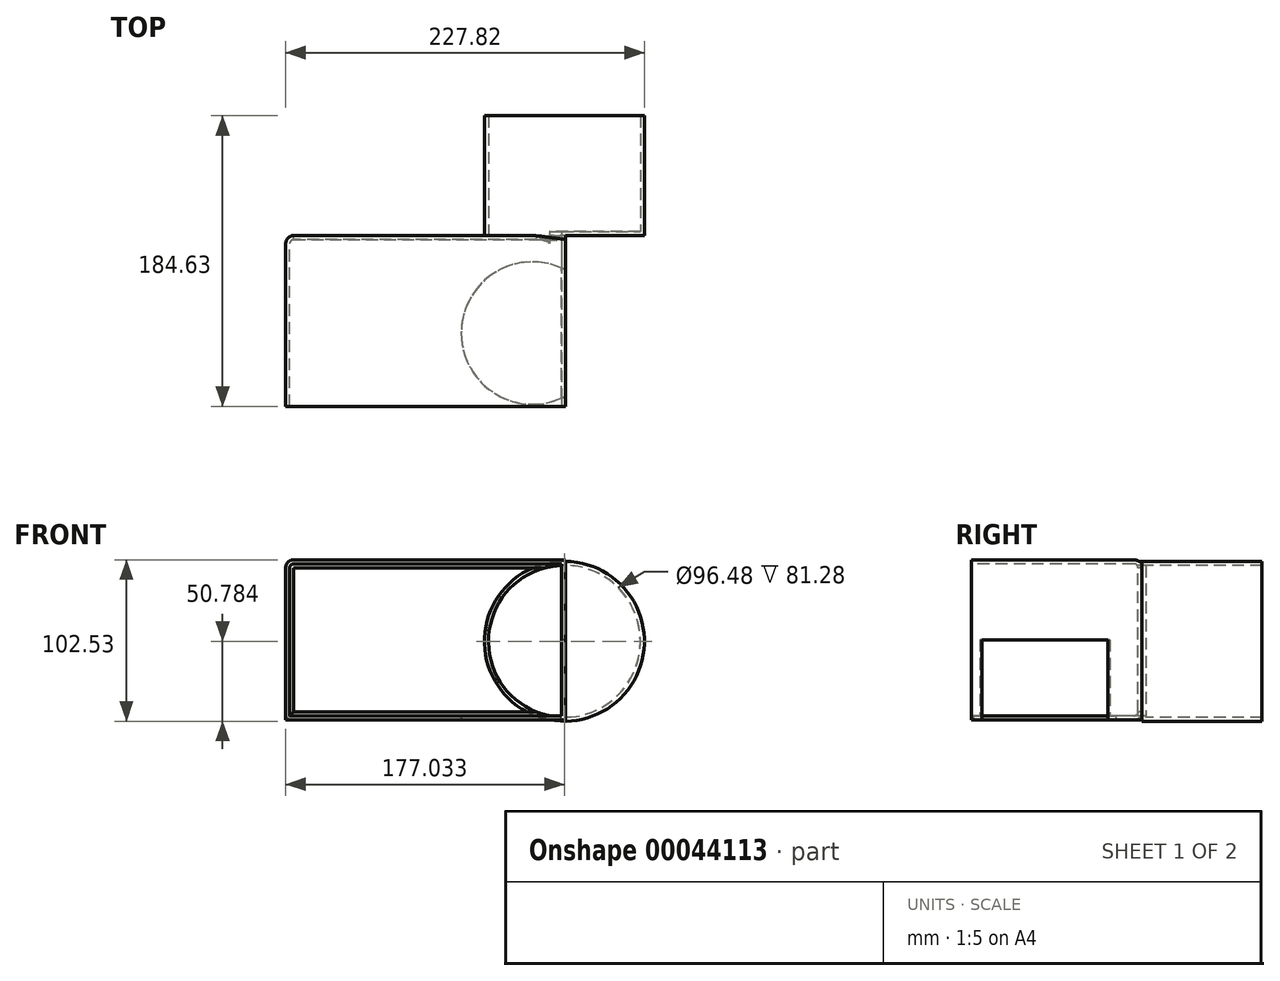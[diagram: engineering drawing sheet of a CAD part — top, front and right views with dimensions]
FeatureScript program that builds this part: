
annotation { "Feature Type Name" : "Feature", "Feature Type Description" : "" }
export const myFeature = defineFeature(function(context is Context, id is Id, definition is map)
    precondition{}
    {
        {
            var Q0;
            Q0=qCreatedBy(makeId("Top.planeOp"),FACE);
            var sketch = newSketch(context, id + "F0", { "sketchPlane" : qUnion([Q0])});
            skLineSegment(sketch, "E0.bottom", {"start": v(-163, 108.43) * mm, "end": v(14.8, 108.43) * mm});
            skLineSegment(sketch, "E0.top", {"start": v(-163, 0) * mm, "end": v(14.8, 0) * mm});
            skLineSegment(sketch, "E0.left", {"start": v(-163, 108.43) * mm, "end": v(-163, 0) * mm});
            skLineSegment(sketch, "E0.right", {"start": v(14.8, 108.43) * mm, "end": v(14.8, 0) * mm});
            skSolve(sketch);
        }
        {
            var Q0;
            Q0=makeQuery(id+"F0.imprint","IMPRINT",FACE,{"disambiguationData":[TD([[makeQuery(id+"F0.imprint","IMPRINT",EDGE,{"derivedFrom":sQuery(id+"F0.wireOp",EDGE,"E0.bottom")}),-1.0]])]});
            extrude(context, id + "F1", {"entities" : qUnion([Q0]), "depth" : 101.6 * mm});
        }
        {
            var Q0;
            Q0=makeQuery(id+"F1.opExtrude","SWEPT_FACE",FACE,{"disambiguationData":[OSD([sQuery(id+"F0.wireOp",EDGE,"E0.bottom")])]});
            var sketch = newSketch(context, id + "F2", { "sketchPlane" : qUnion([Q0])});
            skCircle(sketch, "E1", {"center": v(-14.03, 49.85) * mm, "radius": 50.78 * mm});
            skSolve(sketch);
        }
        {
            var Q0;
            Q0 = qSketchRegion(id + "F2", true);
            extrude(context, id + "F3", {"entities" : qUnion([Q0]), "operationType" : NewBodyOperationType.ADD, "depth" : 76.2 * mm});
        }
        {
            var Q0;
            Q0=makeQuery(id+"F1.opExtrude","CAP_FACE",FACE,{"disambiguationData":[OSD([sQuery(id+"F0.wireOp",EDGE,"E0.bottom"),sQuery(id+"F0.wireOp",EDGE,"E0.top"),sQuery(id+"F0.wireOp",EDGE,"E0.left"),sQuery(id+"F0.wireOp",EDGE,"E0.right")])],"isStart":false});
            var sketch = newSketch(context, id + "F4", { "sketchPlane" : qUnion([Q0])});
            skFitSpline(sketch, "E2", {"points": [v(-81.6, 66.74) * mm, v(-20.34, 86.26) * mm, v(95.36, 39.43) * mm, v(-128.5, 14.59) * mm, v(-81.6, 66.74) * mm]});
            skLineSegment(sketch, "E3", {"start": v(-20.38, 79.14) * mm, "end": v(-20.38, 54.21) * mm, "construction": true});
            skPoint(sketch, "E3.endSnap0", {"position": v(14.8, 54.21) * mm});
            skSolve(sketch);
        }
        {
            var Q0;
            Q0=makeQuery(id+"F1.opExtrude","CAP_EDGE",EDGE,{"disambiguationData":[OSD([sQuery(id+"F0.wireOp",EDGE,"E0.left")])],"isStart":false});
            var Q1;
            Q1=makeQuery(id+"F1.opExtrude","SWEPT_EDGE",EDGE,{"disambiguationData":[OSD([sQuery(id+"F0.wireOp",EDGE,"E0.bottom"),sQuery(id+"F0.wireOp",EDGE,"E0.left")])]});
            var Q2;
            Q2=makeQuery(id+"F1.opExtrude","CAP_EDGE",EDGE,{"disambiguationData":[OSD([sQuery(id+"F0.wireOp",EDGE,"E0.bottom")])],"isStart":false});
            var Q3;
            {var subQ0=sQuery(id+"F0.wireOp",EDGE,"E0.bottom");var subQ1=sQuery(id+"F2.wireOp",EDGE,"E1");var subQ2=sQuery(id+"F0.wireOp",EDGE,"E0.left");Q3=makeQuery(id+"F3.boolean.opBoolean","SPLIT",EDGE,{"disambiguationData":[TD([makeQuery(id+"F1.opExtrude","SWEPT_FACE",FACE,{"disambiguationData":[OSD([subQ0])]}),makeQuery(id+"F1.opExtrude","CAP_FACE",FACE,{"disambiguationData":[OSD([subQ0,sQuery(id+"F0.wireOp",EDGE,"E0.top"),subQ2,sQuery(id+"F0.wireOp",EDGE,"E0.right")])],"isStart":true}),makeQuery(id+"F1.opExtrude","SWEPT_FACE",FACE,{"disambiguationData":[OSD([subQ2])]}),makeQuery(id+"F3.opExtrude","SWEPT_FACE",FACE,{"disambiguationData":[OSD([subQ1])]}),makeQuery(id+"F3.opExtrude","CAP_FACE",FACE,{"disambiguationData":[OSD([subQ1])],"isStart":true})])],"derivedFrom":makeQuery(id+"F1.opExtrude","CAP_EDGE",EDGE,{"disambiguationData":[OSD([subQ0])],"isStart":true})});}
            var Q4;
            {var subQ0=sQuery(id+"F0.wireOp",EDGE,"E0.bottom");var subQ1=sQuery(id+"F2.wireOp",EDGE,"E1");var subQ2=sQuery(id+"F0.wireOp",EDGE,"E0.right");Q4=makeQuery(id+"F3.boolean.opBoolean","SPLIT",EDGE,{"disambiguationData":[TD([makeQuery(id+"F1.opExtrude","SWEPT_FACE",FACE,{"disambiguationData":[OSD([subQ0])]}),makeQuery(id+"F1.opExtrude","CAP_FACE",FACE,{"disambiguationData":[OSD([subQ0,sQuery(id+"F0.wireOp",EDGE,"E0.top"),sQuery(id+"F0.wireOp",EDGE,"E0.left"),subQ2])],"isStart":true}),makeQuery(id+"F1.opExtrude","SWEPT_FACE",FACE,{"disambiguationData":[OSD([subQ2])]}),makeQuery(id+"F3.opExtrude","SWEPT_FACE",FACE,{"disambiguationData":[OSD([subQ1])]}),makeQuery(id+"F3.opExtrude","CAP_FACE",FACE,{"disambiguationData":[OSD([subQ1])],"isStart":true})])],"derivedFrom":makeQuery(id+"F1.opExtrude","CAP_EDGE",EDGE,{"disambiguationData":[OSD([subQ0])],"isStart":true})});}
            var Q5;
            Q5=makeQuery(id+"F52q3UivNeuE0xQ_1.boolean.opBoolean","INTERSECT",EDGE,{"derivedFrom":[makeQuery(id+"F1.opExtrude","CAP_FACE",FACE,{"disambiguationData":[OSD([sQuery(id+"F0.wireOp",EDGE,"E0.bottom"),sQuery(id+"F0.wireOp",EDGE,"E0.top"),sQuery(id+"F0.wireOp",EDGE,"E0.left"),sQuery(id+"F0.wireOp",EDGE,"E0.right")])],"isStart":true}),makeQuery(id+"F52q3UivNeuE0xQ_1.opRevolve","SWEPT_FACE",FACE,{"disambiguationData":[OSD([sQuery(id+"F4.wireOp",EDGE,"E2")])]})]});
            var Q6;
            Q6=makeQuery(id+"F52q3UivNeuE0xQ_1.boolean.opBoolean","INTERSECT",EDGE,{"disambiguationData":[OD(0.0)],"derivedFrom":[makeQuery(id+"F1.opExtrude","CAP_FACE",FACE,{"disambiguationData":[OSD([sQuery(id+"F0.wireOp",EDGE,"E0.bottom"),sQuery(id+"F0.wireOp",EDGE,"E0.top"),sQuery(id+"F0.wireOp",EDGE,"E0.left"),sQuery(id+"F0.wireOp",EDGE,"E0.right")])],"isStart":false}),makeQuery(id+"F52q3UivNeuE0xQ_1.opRevolve","SWEPT_FACE",FACE,{"disambiguationData":[OSD([sQuery(id+"F4.wireOp",EDGE,"E2")])]})]});
            fillet(context, id + "F5", {"entities" : qUnion([Q0, Q1, Q2, Q3, Q4, Q5, Q6]), "radius" : 5.08 * mm, "tangentPropagation" : true, "allowEdgeOverflow" : false});
        }
        {
            var Q0;
            Q0=makeQuery(id+"F3.opExtrude","CAP_FACE",FACE,{"disambiguationData":[OSD([sQuery(id+"F2.wireOp",EDGE,"E1")])],"isStart":false});
            var Q1;
            Q1=makeQuery(id+"F5.opFillet","SPLIT",FACE,{"disambiguationData":[OD(1.0)],"derivedFrom":makeQuery(id+"F1.opExtrude","SWEPT_FACE",FACE,{"disambiguationData":[OSD([sQuery(id+"F0.wireOp",EDGE,"E0.bottom")])]})});
            var Q2;
            Q2=makeQuery(id+"F1.opExtrude","SWEPT_FACE",FACE,{"disambiguationData":[OSD([sQuery(id+"F0.wireOp",EDGE,"E0.top")])]});
            var Q3;
            Q3=makeQuery(id+"F5.opFillet","SPLIT",FACE,{"disambiguationData":[OD(0.0)],"derivedFrom":makeQuery(id+"F1.opExtrude","SWEPT_FACE",FACE,{"disambiguationData":[OSD([sQuery(id+"F0.wireOp",EDGE,"E0.bottom")])]})});
            shell(context, id + "F6", {"entities" : qUnion([Q0, Q1, Q2, Q3]), "thickness" : 2.54 * mm});
        }
        {
            var Q0;
            Q0=makeQuery(id+"F1.opExtrude","CAP_FACE",FACE,{"disambiguationData":[OSD([sQuery(id+"F0.wireOp",EDGE,"E0.bottom"),sQuery(id+"F0.wireOp",EDGE,"E0.top"),sQuery(id+"F0.wireOp",EDGE,"E0.left"),sQuery(id+"F0.wireOp",EDGE,"E0.right")])],"isStart":true});
            var sketch = newSketch(context, id + "F7", { "sketchPlane" : qUnion([Q0])});
            skCircle(sketch, "E4", {"center": v(-6.26, -46.56) * mm, "radius": 45.23 * mm});
            skSolve(sketch);
        }
        {
            var Q0;
            Q0 = qSketchRegion(id + "F7", true);
            extrude(context, id + "F8", {"entities" : qUnion([Q0]), "operationType" : NewBodyOperationType.REMOVE, "oppositeDirection" : true, "depth" : 50.8 * mm});
        }
    });
